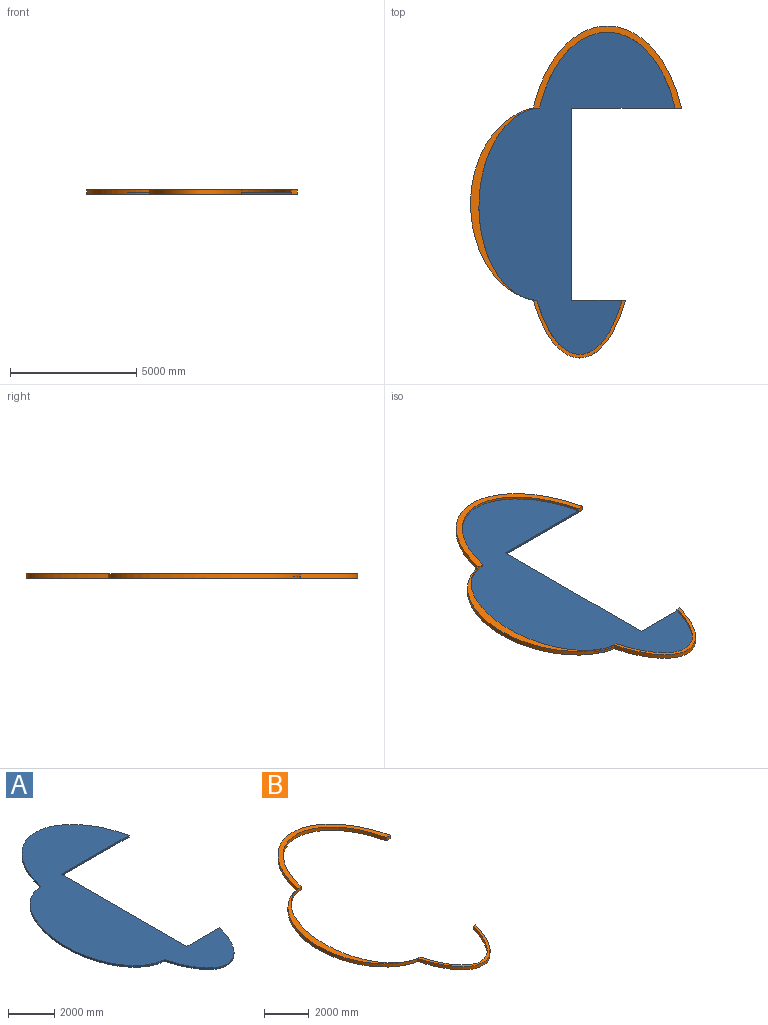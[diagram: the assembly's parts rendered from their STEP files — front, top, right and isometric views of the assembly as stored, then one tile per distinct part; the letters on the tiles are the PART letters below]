
ASSEMBLY  parts=2 mates=1
PART A: 8 faces, bbox 9471.3x14466.6x88.9 mm
  f0: plane 4095.75x88.9mm, normal (0,-1,0), area 364112.2mm2, adj f1,f5,f6,f7
  f1: extruded ~5372.1x3003.55mm, area 770928.1mm2, adj f0,f2,f6,f7
  f2: extruded ~7620x2406.65mm, area 869410.8mm2, adj f1,f3,f6,f7
  f3: extruded ~3378.2x2146.3mm, area 516363.8mm2, adj f2,f4,f6,f7
  f4: plane 1993.9x88.9mm, normal (0,1,0), area 177257.7mm2, adj f3,f5,f6,f7
  f5: plane 7620x88.9mm, normal (1,0,0), area 677418mm2, adj f0,f4,f6,f7
  f6: plane 14466.63x9471.34mm, normal (0,0,1), area 41009804.9mm2, adj f0,f1,f2,f3,f4,f5
  f7: plane 14466.63x9471.34mm, normal (0,0,-1), area 41009804.9mm2, adj f0,f1,f2,f3,f4,f5
PART B: 10 faces, bbox 9796.6x14988.1x177.8 mm
  f0: plane 177.8x139.7mm, normal (0,1,0), area 24838.7mm2, adj f1,f7,f8,f9
  f1: extruded ~3378.2x2146.3mm, area 1032727.5mm2, adj f0,f2,f8,f9
  f2: extruded ~7620x2406.65mm, area 1738821.6mm2, adj f1,f3,f8,f9
  f3: extruded ~5372.1x3003.55mm, area 1541856.2mm2, adj f2,f4,f8,f9
  f4: plane 247.65x177.8mm, normal (0,-1,0), area 44032.2mm2, adj f3,f5,f8,f9
  f5: extruded ~5867.4x3251.2mm, area 1675691.1mm2, adj f4,f6,f8,f9
  f6: extruded ~7620x2489.2mm, area 1747020.2mm2, adj f5,f7,f8,f9
  f7: extruded ~3657.6x2286mm, area 1107091.5mm2, adj f0,f6,f8,f9
  f8: plane 14988.1x9796.56mm, normal (0,0,1), area 4788846.7mm2, adj f0,f1,f2,f3,f4,f5,f6,f7
  f9: plane 14988.1x9796.56mm, normal (0,0,-1), area 4788846.7mm2, adj f0,f1,f2,f3,f4,f5,f6,f7
PLACE A t=(-9848.18,855.81,0)mm
PLACE B t=(-9848.18,855.81,0)mm
MATE fastened B.f9 <-> A.f7  axis (0,0,-1) through (1993.9,-3810,0)mm
